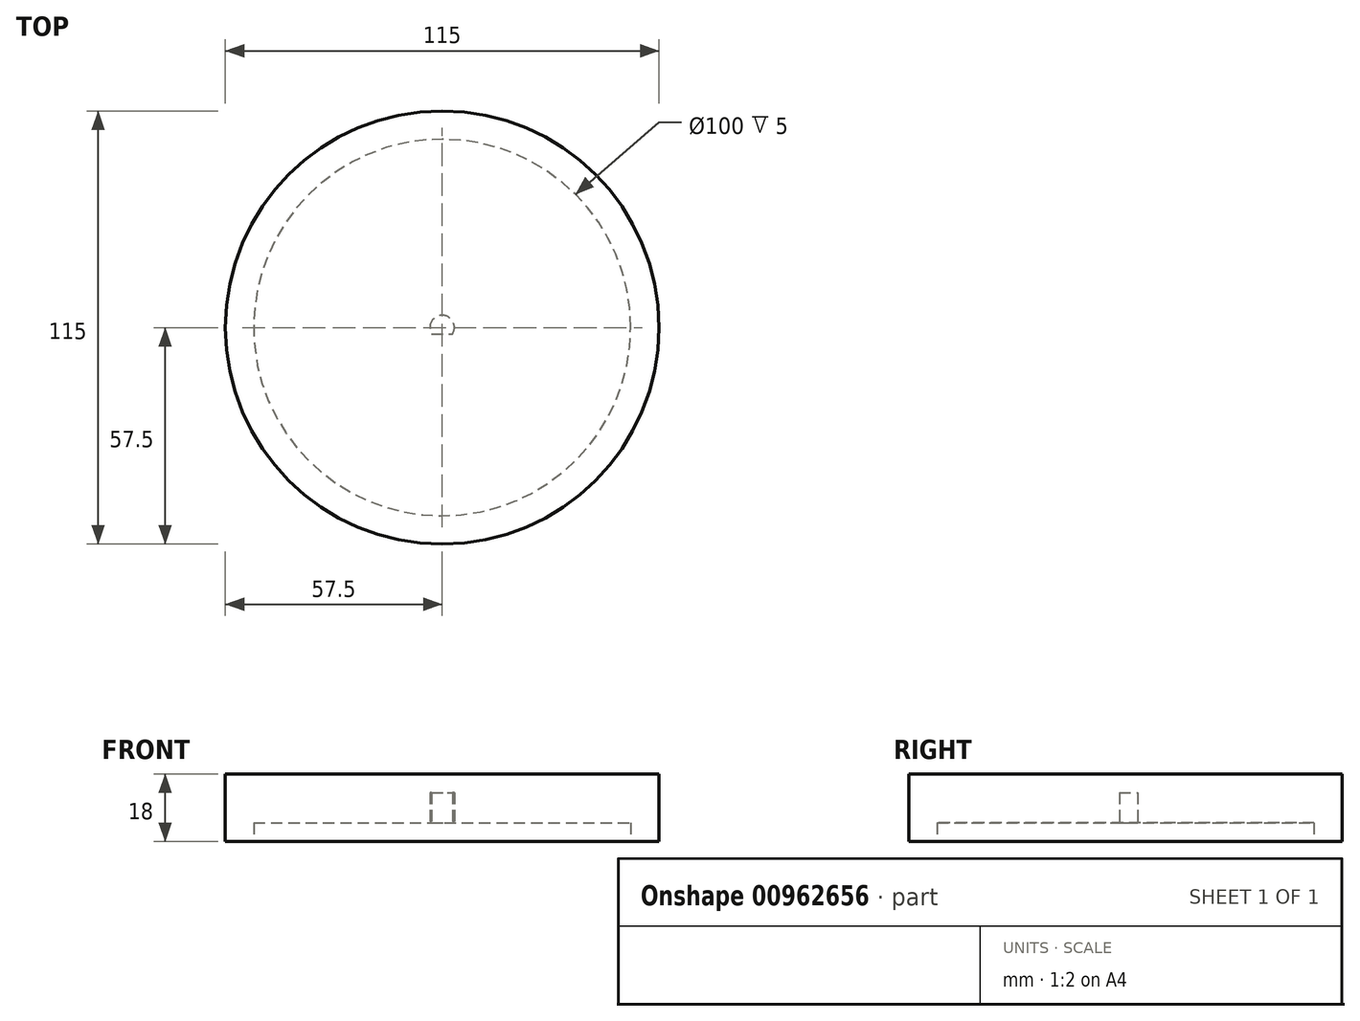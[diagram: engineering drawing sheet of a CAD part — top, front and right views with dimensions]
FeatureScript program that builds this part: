
annotation { "Feature Type Name" : "Feature", "Feature Type Description" : "" }
export const myFeature = defineFeature(function(context is Context, id is Id, definition is map)
    precondition{}
    {
        {
            var Q0;
            Q0=qCreatedBy(makeId("Top.planeOp"),FACE);
            var sketch = newSketch(context, id + "F0", { "sketchPlane" : qUnion([Q0])});
            skCircle(sketch, "E0", {"center": v(0, 0) * mm, "radius": 57.5 * mm});
            skSolve(sketch);
        }
        {
            var Q0;
            Q0 = qSketchRegion(id + "F0", true);
            extrude(context, id + "F1", {"entities" : qUnion([Q0]), "depth" : 18 * mm, "offsetDistance" : 25 * mm});
        }
        {
            var Q0;
            Q0=makeQuery(id+"F1.opExtrude","CAP_FACE",FACE,{"disambiguationData":[OSD([sQuery(id+"F0.wireOp",EDGE,"E0")])],"isStart":true});
            var sketch = newSketch(context, id + "F2", { "sketchPlane" : qUnion([Q0])});
            skCircle(sketch, "E1", {"center": v(0, 0) * mm, "radius": 50 * mm});
            skSolve(sketch);
        }
        {
            var Q0;
            Q0=makeQuery(id+"F2.imprint","IMPRINT",FACE,{"disambiguationData":[TD([[makeQuery(id+"F2.imprint","IMPRINT",EDGE,{"derivedFrom":sQuery(id+"F2.wireOp",EDGE,"E1")}),1.0]])]});
            extrude(context, id + "F3", {"entities" : qUnion([Q0]), "operationType" : NewBodyOperationType.REMOVE, "oppositeDirection" : true, "depth" : 5 * mm, "offsetDistance" : 25 * mm});
        }
        {
            var Q0;
            Q0=makeQuery(id+"F3.boolean.opBoolean","COPY",FACE,{"derivedFrom":makeQuery(id+"F3.opExtrude","CAP_FACE",FACE,{"disambiguationData":[OSD([sQuery(id+"F2.wireOp",EDGE,"E1")])],"isStart":false})});
            var sketch = newSketch(context, id + "F4", { "sketchPlane" : qUnion([Q0])});
            skCircle(sketch, "E2", {"center": v(0, 0) * mm, "radius": 3.25 * mm});
            skLineSegment(sketch, "E3", {"start": v(-2.8, 1.65) * mm, "end": v(2.8, 1.65) * mm});
            skSolve(sketch);
        }
        {
            var Q0;
            {var subQ0=sQuery(id+"F4.wireOp",EDGE,"E3");Q0=makeQuery(id+"F4.imprint","IMPRINT",FACE,{"disambiguationData":[TD([[makeQuery(id+"F4.imprint","IMPRINT",EDGE,{"derivedFrom":subQ0}),-1.0]])]});}
            extrude(context, id + "F5", {"entities" : qUnion([Q0]), "operationType" : NewBodyOperationType.REMOVE, "oppositeDirection" : true, "depth" : 8 * mm, "offsetDistance" : 25 * mm});
        }
    });
